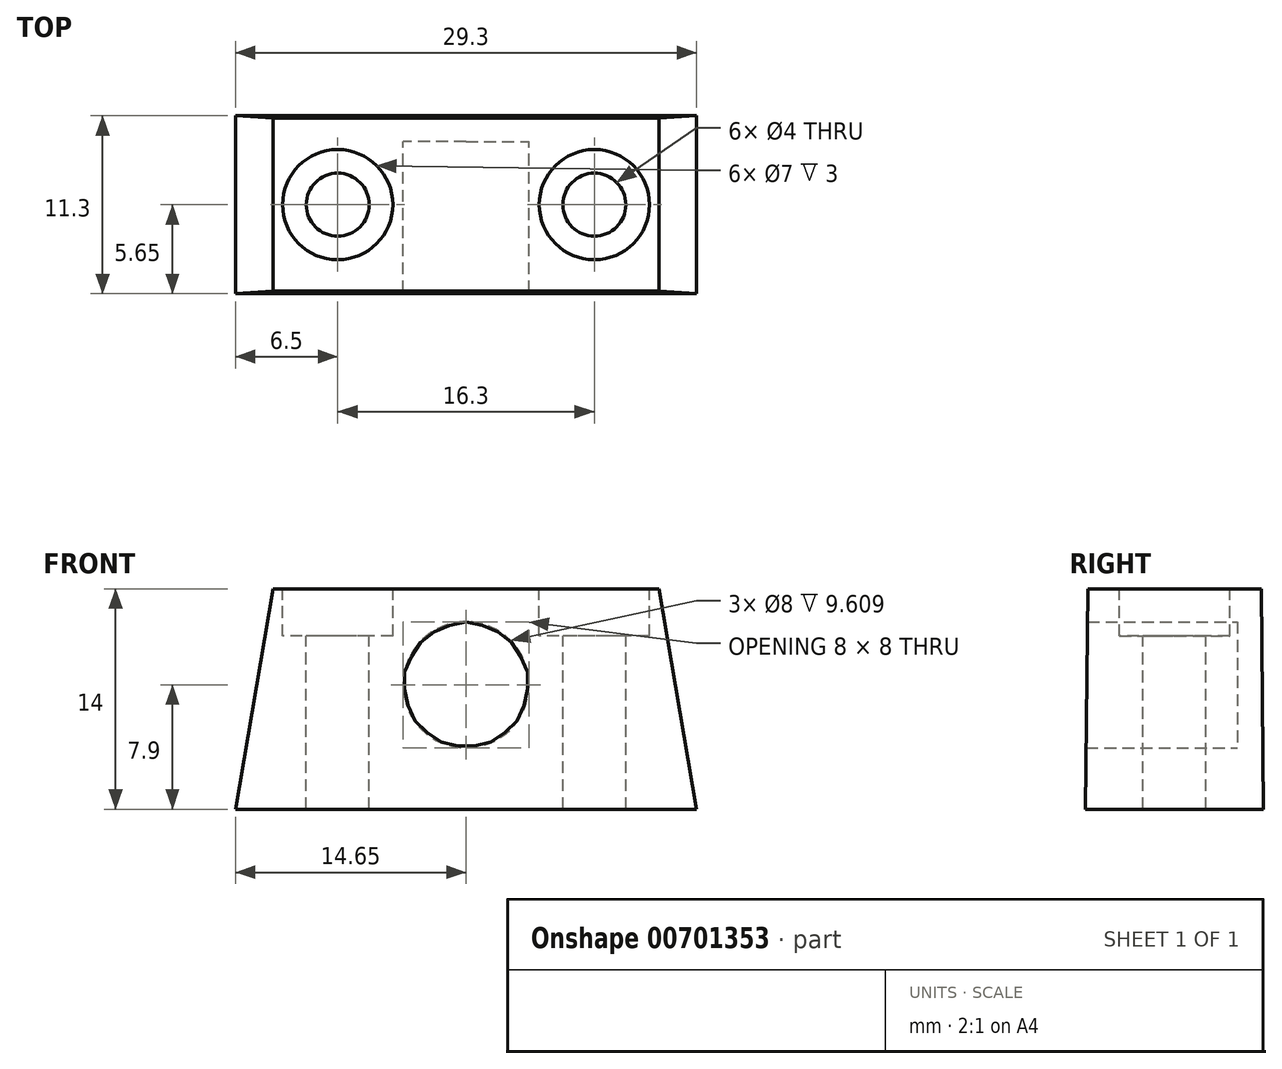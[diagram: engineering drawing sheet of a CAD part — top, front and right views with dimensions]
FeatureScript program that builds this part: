
annotation { "Feature Type Name" : "Feature", "Feature Type Description" : "" }
export const myFeature = defineFeature(function(context is Context, id is Id, definition is map)
    precondition{}
    {
        {
            var Q0;
            Q0=qCreatedBy(makeId("Top.planeOp"),FACE);
            var sketch = newSketch(context, id + "F0", { "sketchPlane" : qUnion([Q0])});
            skLineSegment(sketch, "E0.bottom", {"start": v(-14.65, -5.65) * mm, "end": v(14.65, -5.65) * mm});
            skLineSegment(sketch, "E0.top", {"start": v(-14.65, 5.65) * mm, "end": v(14.65, 5.65) * mm});
            skLineSegment(sketch, "E0.left", {"start": v(-14.65, -5.65) * mm, "end": v(-14.65, 5.65) * mm});
            skLineSegment(sketch, "E0.right", {"start": v(14.65, -5.65) * mm, "end": v(14.65, 5.65) * mm});
            skPoint(sketch, "E0.middle", {"position": v(0, 0) * mm});
            skSolve(sketch);
        }
        {
            var Q0;
            Q0=makeQuery(id+"F0.imprint","IMPRINT",FACE,{"disambiguationData":[TD([[makeQuery(id+"F0.imprint","IMPRINT",EDGE,{"derivedFrom":sQuery(id+"F0.wireOp",EDGE,"E0.bottom")}),1.0]])]});
            cPlane(context, id + "F1", {"entities" : qUnion([Q0]), "cplaneType" : CPlaneType.OFFSET, "offset" : 14 * mm, "width" : 150 * mm, "height" : 150 * mm});
        }
        {
            var Q0;
            Q0=qCreatedBy(id+"F1.planeOp",FACE);
            var sketch = newSketch(context, id + "F2", { "sketchPlane" : qUnion([Q0])});
            skLineSegment(sketch, "E1.bottom", {"start": v(-12.25, -5.5) * mm, "end": v(12.25, -5.5) * mm});
            skLineSegment(sketch, "E1.top", {"start": v(-12.25, 5.5) * mm, "end": v(12.25, 5.5) * mm});
            skLineSegment(sketch, "E1.left", {"start": v(-12.25, -5.5) * mm, "end": v(-12.25, 5.5) * mm});
            skLineSegment(sketch, "E1.right", {"start": v(12.25, -5.5) * mm, "end": v(12.25, 5.5) * mm});
            skPoint(sketch, "E1.middle", {"position": v(0, 0) * mm});
            skSolve(sketch);
        }
        {
            var Q0;
            Q0=makeQuery(id+"F0.imprint","IMPRINT",FACE,{"disambiguationData":[TD([[makeQuery(id+"F0.imprint","IMPRINT",EDGE,{"derivedFrom":sQuery(id+"F0.wireOp",EDGE,"E0.bottom")}),1.0]])]});
            var Q1;
            Q1=makeQuery(id+"F2.imprint","IMPRINT",FACE,{"disambiguationData":[TD([[makeQuery(id+"F2.imprint","IMPRINT",EDGE,{"derivedFrom":sQuery(id+"F2.wireOp",EDGE,"E1.bottom")}),1.0]])]});
            loft(context, id + "F3", {"sheetProfilesArray" : [{ "sheetProfileEntities" : qUnion([Q0]) }, { "sheetProfileEntities" : qUnion([Q1]) }]});
        }
        {
            var Q0;
            Q0=makeQuery(id+"F0.imprint","IMPRINT",FACE,{"disambiguationData":[TD([[makeQuery(id+"F0.imprint","IMPRINT",EDGE,{"derivedFrom":sQuery(id+"F0.wireOp",EDGE,"E0.bottom")}),1.0]])]});
            var sketch = newSketch(context, id + "F4", { "sketchPlane" : qUnion([Q0])});
            skLineSegment(sketch, "E2.bottom", {"start": v(-14.65, -1) * mm, "end": v(-9.46, -1) * mm});
            skLineSegment(sketch, "E2.top", {"start": v(-14.65, 1) * mm, "end": v(-9.46, 1) * mm});
            skLineSegment(sketch, "E2.left", {"start": v(-14.65, -1) * mm, "end": v(-14.65, 1) * mm});
            skLineSegment(sketch, "E2.right", {"start": v(14.65, -1) * mm, "end": v(14.65, 1) * mm});
            skPoint(sketch, "E2.middle", {"position": v(0, 0) * mm});
            skLineSegment(sketch, "E3.0", {"start": v(14.65, -5.65) * mm, "end": v(14.65, 5.65) * mm});
            skLineSegment(sketch, "E4.0", {"start": v(-14.65, -5.65) * mm, "end": v(-14.65, 5.65) * mm});
            skLineSegment(sketch, "E5.0", {"start": v(-14.65, 5.65) * mm, "end": v(14.65, 5.65) * mm});
            skLineSegment(sketch, "E6.0", {"start": v(-14.65, -5.65) * mm, "end": v(14.65, -5.65) * mm});
            skPoint(sketch, "E7", {"position": v(14.65, 0) * mm});
            skPoint(sketch, "E8", {"position": v(-14.65, 0) * mm});
            skLineSegment(sketch, "E9", {"start": v(14.65, 0) * mm, "end": v(-14.65, 0) * mm, "construction": true});
            skPoint(sketch, "E10", {"position": v(8.15, 0) * mm});
            skCircle(sketch, "E11", {"center": v(8.15, 0) * mm, "radius": 1.65 * mm});
            skLineSegment(sketch, "E12", {"start": v(0, 5.65) * mm, "end": v(0, -5.65) * mm, "construction": true});
            skLineSegment(sketch, "E13.trimOffspring", {"start": v(9.46, 1) * mm, "end": v(14.65, 1) * mm});
            skLineSegment(sketch, "E14.trimOffspring", {"start": v(9.46, -1) * mm, "end": v(14.65, -1) * mm});
            skCircle(sketch, "E15.MirrorC", {"center": v(-8.15, 0) * mm, "radius": 1.65 * mm});
            skLineSegment(sketch, "E16.trimOffspring", {"start": v(-6.84, 1) * mm, "end": v(6.84, 1) * mm});
            skLineSegment(sketch, "E17.trimOffspring", {"start": v(-6.84, -1) * mm, "end": v(6.84, -1) * mm});
            skSolve(sketch);
        }
        {
            var Q0;
            Q0=makeQuery(id+"F2.imprint","IMPRINT",FACE,{"disambiguationData":[TD([[makeQuery(id+"F2.imprint","IMPRINT",EDGE,{"derivedFrom":sQuery(id+"F2.wireOp",EDGE,"E1.bottom")}),1.0]])]});
            var sketch = newSketch(context, id + "F5", { "sketchPlane" : qUnion([Q0])});
            skPoint(sketch, "E18.0", {"position": v(8.15, 0) * mm});
            skPoint(sketch, "E19.0", {"position": v(-8.15, 0) * mm});
            skSolve(sketch);
        }
        {
            var Q0;
            Q0=sQuery(id+"F5.wireOp",VERTEX,"E19.0");
            var Q1;
            Q1=sQuery(id+"F5.wireOp",VERTEX,"E18.0");
            var Q2;
            Q2=makeQuery(id+"F3.opLoft","SWEPT_BODY",BODY,{"disambiguationData":[OSD([makeQuery(id+"F0.imprint","IMPRINT",FACE,{"disambiguationData":[TD([[makeQuery(id+"F0.imprint","IMPRINT",EDGE,{"derivedFrom":sQuery(id+"F0.wireOp",EDGE,"E0.bottom")}),1.0]])]}),makeQuery(id+"F2.imprint","IMPRINT",FACE,{"disambiguationData":[TD([[makeQuery(id+"F2.imprint","IMPRINT",EDGE,{"derivedFrom":sQuery(id+"F2.wireOp",EDGE,"E1.bottom")}),1.0]])]})])]});
            hole(context, id + "F6", {"style" : HoleStyle.C_BORE, "endStyle" : HoleEndStyle.THROUGH, "standardTappedOrClearance" : lookupTablePath({ "fit" : "Normal", "standard" : "Custom", "size" : "5", "type" : "Drilled" }), "standardBlindInLast" : lookupTablePath({ "fit" : "Standard", "standard" : "Custom", "size" : "5", "type" : "Drilled" }), "holeDiameter" : 4 * mm, "cBoreDiameter" : 7 * mm, "cBoreDepth" : 3 * mm, "majorDiameter" : 5 * mm, "isTappedThrough" : true, "tappedDepth" : 12 * mm, "tapClearance" : 3, "locations" : qUnion([Q0, Q1]), "scope" : qUnion([Q2])});
        }
        {
            var Q0;
            Q0=qCreatedBy(makeId("Front.planeOp"),FACE);
            var sketch = newSketch(context, id + "F7", { "sketchPlane" : qUnion([Q0])});
            skCircle(sketch, "E20", {"center": v(0, 7.9) * mm, "radius": 4 * mm});
            skLineSegment(sketch, "E21", {"start": v(0, 0) * mm, "end": v(0, 15.56) * mm, "construction": true});
            skSolve(sketch);
        }
        {
            var Q0;
            Q0=makeQuery(id+"F7.imprint","IMPRINT",FACE,{"disambiguationData":[TD([[makeQuery(id+"F7.imprint","IMPRINT",EDGE,{"derivedFrom":sQuery(id+"F7.wireOp",EDGE,"E20")}),1.0]])]});
            var Q1;
            Q1=sQuery(id+"F7.wireOp",EDGE,"E20");
            extrude(context, id + "F8", {"entities" : qUnion([Q0]), "operationType" : NewBodyOperationType.REMOVE, "surfaceEntities" : qUnion([Q1]), "endBound" : BoundingType.THROUGH_ALL, "depth" : 22.62 * mm, "offsetDistance" : 25 * mm, "hasSecondDirection" : true, "secondDirectionOppositeDirection" : true, "secondDirectionDepth" : 4 * mm});
        }
    });
